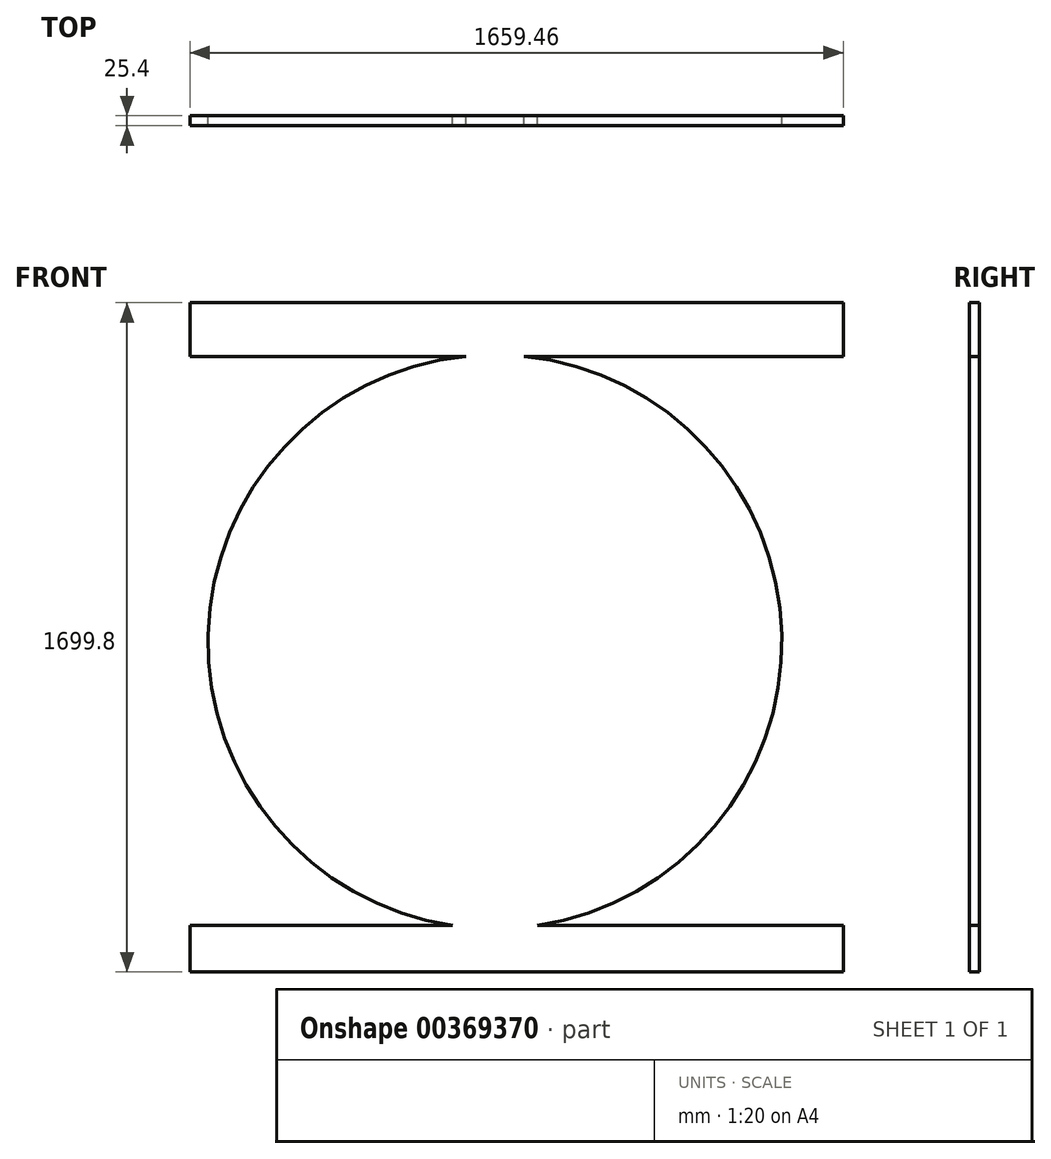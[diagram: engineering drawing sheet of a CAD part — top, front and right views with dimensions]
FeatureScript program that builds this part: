
annotation { "Feature Type Name" : "Feature", "Feature Type Description" : "" }
export const myFeature = defineFeature(function(context is Context, id is Id, definition is map)
    precondition{}
    {
        {
            var Q0;
            Q0=qCreatedBy(makeId("Front.planeOp"),FACE);
            var sketch = newSketch(context, id + "F0", { "sketchPlane" : qUnion([Q0])});
            skCircle(sketch, "E0", {"center": v(0, 0) * mm, "radius": 728.89 * mm});
            skLineSegment(sketch, "E1.bottom", {"start": v(-774.28, 861.15) * mm, "end": v(885.18, 861.15) * mm});
            skLineSegment(sketch, "E1.top", {"start": v(-774.28, 725.18) * mm, "end": v(885.18, 725.18) * mm});
            skLineSegment(sketch, "E1.left", {"start": v(-774.28, 861.15) * mm, "end": v(-774.28, 725.18) * mm});
            skLineSegment(sketch, "E1.right", {"start": v(885.18, 861.15) * mm, "end": v(885.18, 725.18) * mm});
            skLineSegment(sketch, "E2.bottom", {"start": v(-774.28, -720.9) * mm, "end": v(885.18, -720.9) * mm});
            skLineSegment(sketch, "E2.top", {"start": v(-774.28, -838.65) * mm, "end": v(885.18, -838.65) * mm});
            skLineSegment(sketch, "E2.left", {"start": v(-774.28, -720.9) * mm, "end": v(-774.28, -838.65) * mm});
            skLineSegment(sketch, "E2.right", {"start": v(885.18, -720.9) * mm, "end": v(885.18, -838.65) * mm});
            skSolve(sketch);
        }
        {
            var Q0;
            Q0=makeQuery(id+"F0.imprint","IMPRINT",FACE,{"disambiguationData":[TD([[makeQuery(id+"F0.imprint","IMPRINT",EDGE,{"derivedFrom":sQuery(id+"F0.wireOp",EDGE,"E1.bottom")}),-1.0]])]});
            extrude(context, id + "F1", {"entities" : qUnion([Q0]), "depth" : 25.4 * mm});
        }
        {
            var Q0;
            Q0=sQuery(id+"F0.wireOp",EDGE,"E0");
            extrude(context, id + "F2", {"bodyType" : ToolBodyType.SURFACE, "surfaceEntities" : qUnion([Q0]), "depth" : 50.8 * mm});
        }
        {
            var Q0;
            Q0 = qSketchRegion(id + "F0", true);
            extrude(context, id + "F3", {"entities" : qUnion([Q0]), "operationType" : NewBodyOperationType.ADD, "depth" : 25.4 * mm});
        }
    });
